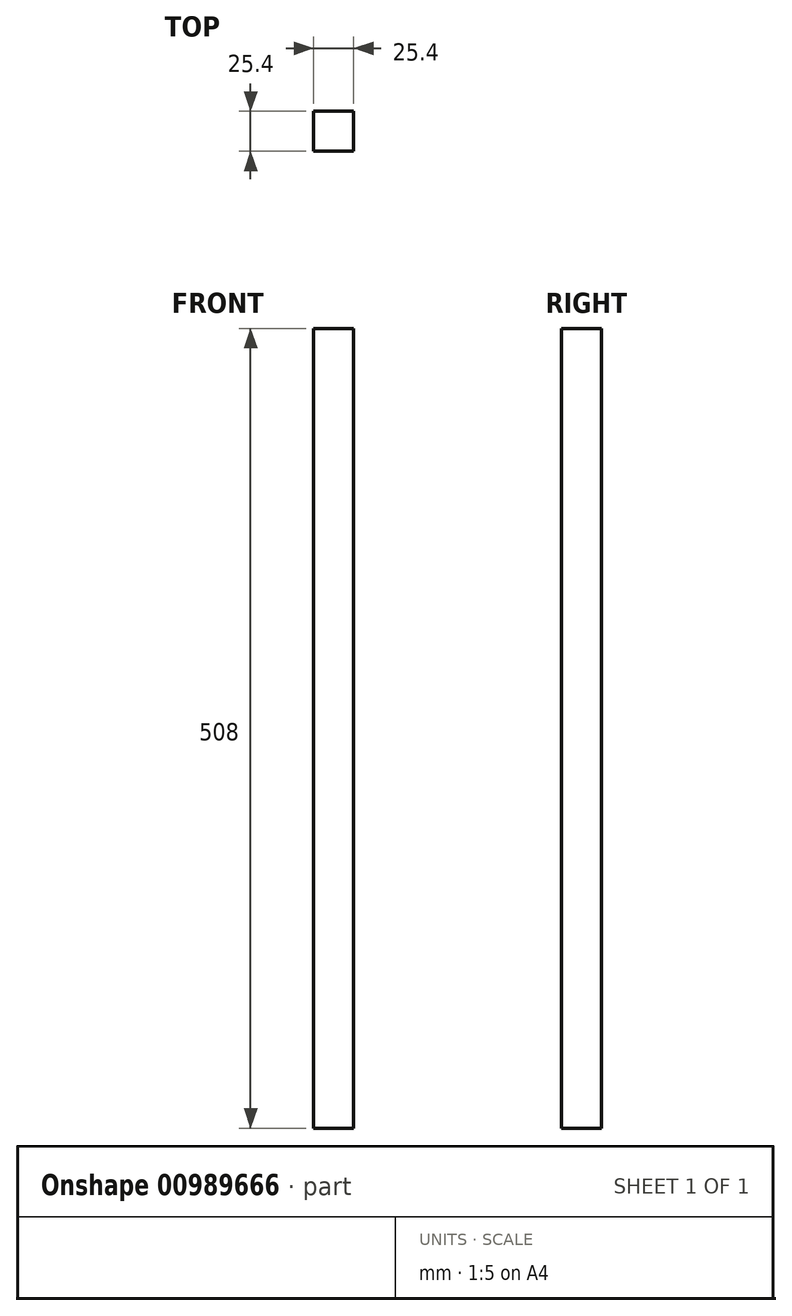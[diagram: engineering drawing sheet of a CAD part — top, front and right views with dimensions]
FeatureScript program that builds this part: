
annotation { "Feature Type Name" : "Feature", "Feature Type Description" : "" }
export const myFeature = defineFeature(function(context is Context, id is Id, definition is map)
    precondition{}
    {
        {
            var Q0;
            Q0=qCreatedBy(makeId("Top.planeOp"),FACE);
            var sketch = newSketch(context, id + "F0", { "sketchPlane" : qUnion([Q0])});
            skLineSegment(sketch, "E0.bottom", {"start": v(0, 0) * mm, "end": v(25.4, 0) * mm});
            skLineSegment(sketch, "E0.top", {"start": v(0, 25.4) * mm, "end": v(25.4, 25.4) * mm});
            skLineSegment(sketch, "E0.left", {"start": v(0, 0) * mm, "end": v(0, 25.4) * mm});
            skLineSegment(sketch, "E0.right", {"start": v(25.4, 0) * mm, "end": v(25.4, 25.4) * mm});
            skSolve(sketch);
        }
        {
            var Q0;
            Q0=makeQuery(id+"F0.imprint","IMPRINT",FACE,{"disambiguationData":[TD([[makeQuery(id+"F0.imprint","IMPRINT",EDGE,{"derivedFrom":sQuery(id+"F0.wireOp",EDGE,"E0.bottom")}),1.0]])]});
            extrude(context, id + "F1", {"entities" : qUnion([Q0]), "depth" : 508 * mm, "offsetDistance" : 25.4 * mm});
        }
    });
